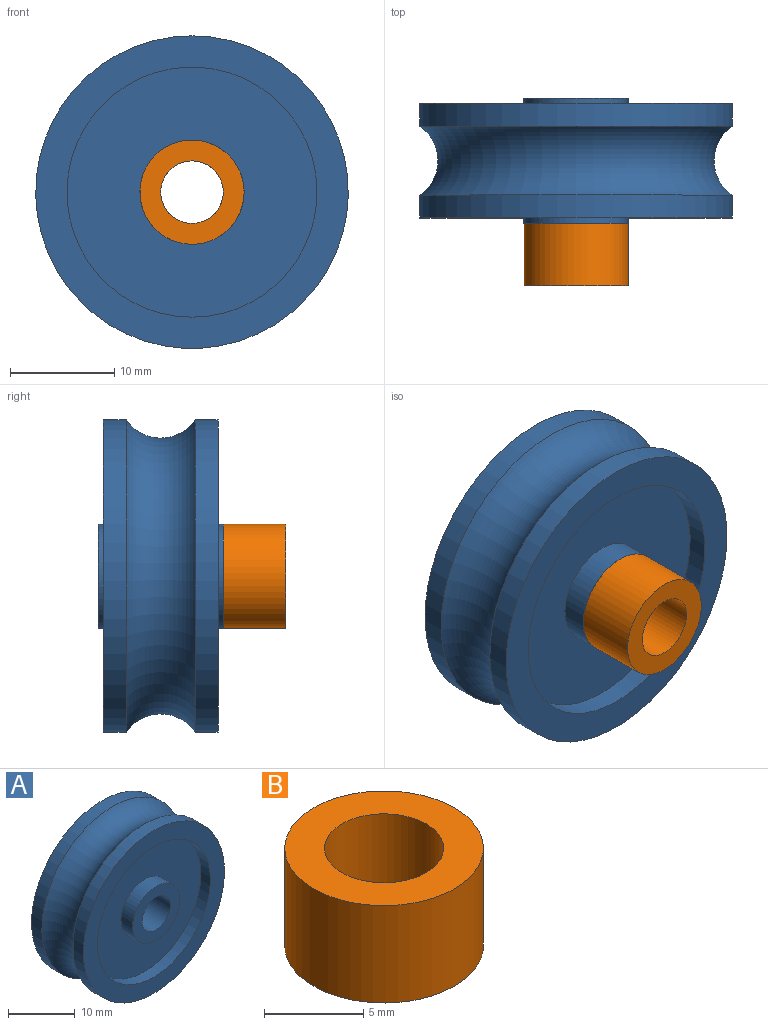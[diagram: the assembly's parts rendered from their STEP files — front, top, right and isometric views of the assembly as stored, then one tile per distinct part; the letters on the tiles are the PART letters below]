
ASSEMBLY  parts=2 mates=1
PART A: 14 faces, bbox 37.3x12x37.3 mm
  f0: torus R=17.25mm, axis (0,1,0), area 677.8mm2, adj f1,f8
  f1: cylinder r=15mm len=30mm, axis (0,1,0), area 206.7mm2, adj f0,f2
  f2: plane 30x30mm, normal (0,-1,0), area 254.5mm2, adj f1,f3
  f3: cylinder r=12mm len=24mm, axis (0,-1,0), area 150.8mm2, adj f2,f4
  f4: plane 24x24mm, normal (0,-1,0), area 373.8mm2, adj f3,f7
  f5: cylinder r=3mm len=12mm, axis (0,1,0), area 226.2mm2, adj f6,f12
  f6: plane 10x10mm, normal (0,-1,0), area 50.3mm2, adj f5,f7
  f7: cylinder r=5mm len=10mm, axis (0,1,0), area 78.5mm2, adj f4,f6
  f8: cylinder r=15mm len=30mm, axis (0,-1,0), area 206.7mm2, adj f0,f9
  f9: plane 30x30mm, normal (0,1,0), area 254.5mm2, adj f8,f10
  f10: cylinder r=12mm len=24mm, axis (0,1,0), area 150.8mm2, adj f9,f11
  f11: plane 24x24mm, normal (0,1,0), area 373.8mm2, adj f10,f13
  f12: plane 10x10mm, normal (0,1,0), area 50.3mm2, adj f5,f13
  f13: cylinder r=5mm len=10mm, axis (0,-1,0), area 78.5mm2, adj f11,f12
PART B: 4 faces, bbox 10x10x6 mm
  f0: cylinder r=3mm len=6mm, axis (0,0,-1), area 113.1mm2, adj f2,f3
  f1: cylinder r=5mm len=10mm, axis (0,0,-1), area 188.5mm2, adj f2,f3
  f2: plane 10x10mm, normal (0,0,1), area 50.3mm2, adj f0,f1
  f3: plane 10x10mm, normal (0,0,-1), area 50.3mm2, adj f0,f1
PLACE A t=(-9.98,-1.96,5.71)mm
PLACE B rot(axis=(-1,0,0),90deg) t=(-1.1,-13.96,-50.77)mm
MATE fastened B.f0 <-> A.f5  axis (0,1,0) through (-9.98,-7.96,5.71)mm
